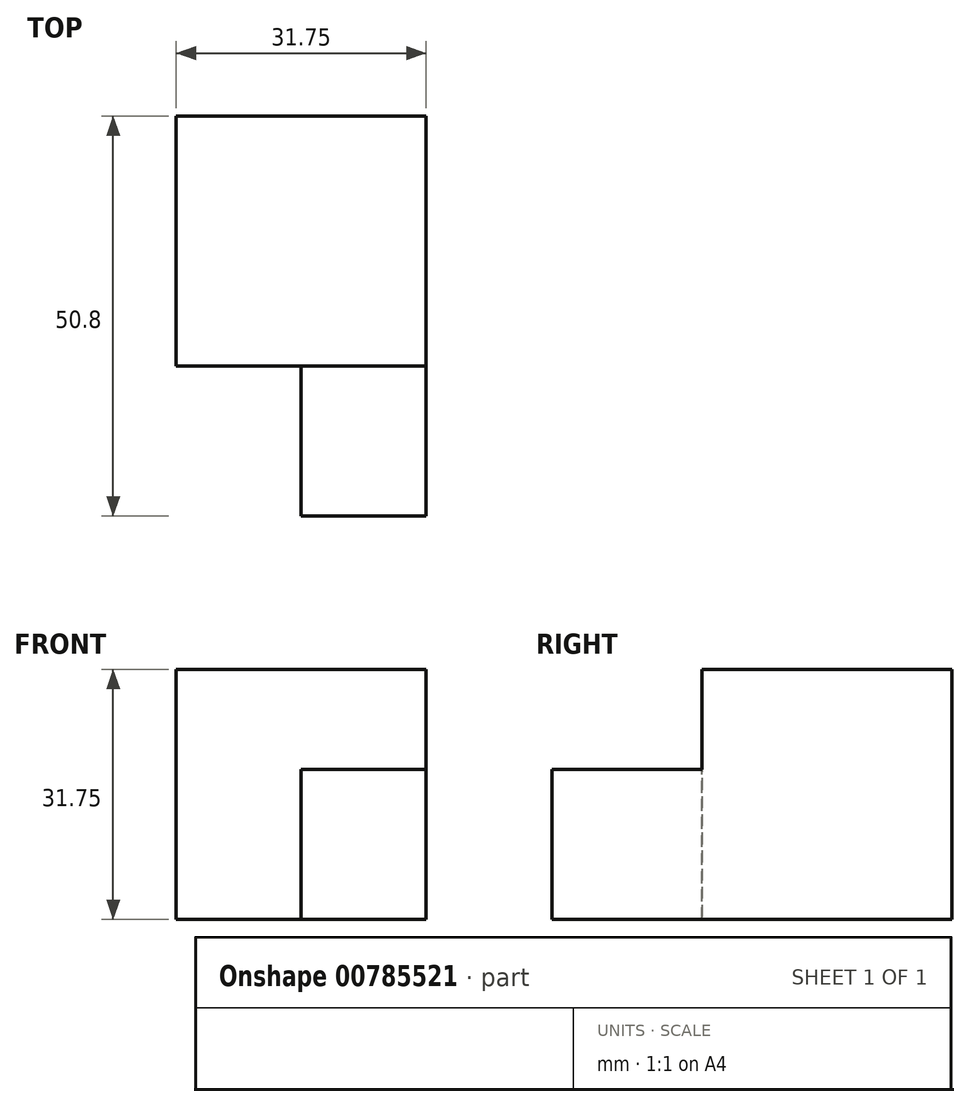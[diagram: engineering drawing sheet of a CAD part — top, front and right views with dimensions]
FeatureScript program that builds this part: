
annotation { "Feature Type Name" : "Feature", "Feature Type Description" : "" }
export const myFeature = defineFeature(function(context is Context, id is Id, definition is map)
    precondition{}
    {
        {
            var Q0;
            Q0=qCreatedBy(makeId("Front.planeOp"),FACE);
            var sketch = newSketch(context, id + "F0", { "sketchPlane" : qUnion([Q0])});
            skLineSegment(sketch, "E0", {"start": v(0, 0) * mm, "end": v(31.75, 0) * mm});
            skLineSegment(sketch, "E1", {"start": v(31.75, 0) * mm, "end": v(31.75, 31.75) * mm});
            skLineSegment(sketch, "E2", {"start": v(31.75, 31.75) * mm, "end": v(0, 31.75) * mm});
            skLineSegment(sketch, "E3", {"start": v(0, 31.75) * mm, "end": v(0, 0) * mm});
            skSolve(sketch);
        }
        {
            var Q0;
            Q0=makeQuery(id+"F0.imprint","IMPRINT",FACE,{"disambiguationData":[TD([[makeQuery(id+"F0.imprint","IMPRINT",EDGE,{"derivedFrom":sQuery(id+"F0.wireOp",EDGE,"E0")}),1.0]])]});
            extrude(context, id + "F1", {"entities" : qUnion([Q0]), "depth" : 50.8 * mm, "offsetDistance" : 25.4 * mm});
        }
        {
            var Q0;
            Q0=makeQuery(id+"F1.opExtrude","CAP_FACE",FACE,{"disambiguationData":[OSD([sQuery(id+"F0.wireOp",EDGE,"E0"),sQuery(id+"F0.wireOp",EDGE,"E1"),sQuery(id+"F0.wireOp",EDGE,"E2"),sQuery(id+"F0.wireOp",EDGE,"E3")])],"isStart":false});
            var sketch = newSketch(context, id + "F2", { "sketchPlane" : qUnion([Q0])});
            skLineSegment(sketch, "E4", {"start": v(31.75, 0) * mm, "end": v(31.75, 19.05) * mm});
            skLineSegment(sketch, "E5", {"start": v(31.75, 19.05) * mm, "end": v(0, 19.05) * mm});
            skSolve(sketch);
        }
        {
            var Q0;
            {var subQ0=sQuery(id+"F2.wireOp",EDGE,"E5");Q0=makeQuery(id+"F2.imprint","IMPRINT",FACE,{"disambiguationData":[TD([[makeQuery(id+"F2.imprint","IMPRINT",EDGE,{"derivedFrom":subQ0}),-1.0]])]});}
            extrude(context, id + "F3", {"entities" : qUnion([Q0]), "operationType" : NewBodyOperationType.REMOVE, "oppositeDirection" : true, "depth" : 19.05 * mm, "offsetDistance" : 25.4 * mm});
        }
        {
            var Q0;
            Q0=makeQuery(id+"F1.opExtrude","CAP_FACE",FACE,{"disambiguationData":[OSD([sQuery(id+"F0.wireOp",EDGE,"E0"),sQuery(id+"F0.wireOp",EDGE,"E1"),sQuery(id+"F0.wireOp",EDGE,"E2"),sQuery(id+"F0.wireOp",EDGE,"E3")])],"isStart":false});
            var sketch = newSketch(context, id + "F4", { "sketchPlane" : qUnion([Q0])});
            skLineSegment(sketch, "E6", {"start": v(31.75, 0) * mm, "end": v(15.88, 0) * mm});
            skLineSegment(sketch, "E7", {"start": v(15.88, 0) * mm, "end": v(15.88, 19.05) * mm});
            skSolve(sketch);
        }
        {
            var Q0;
            {var subQ0=sQuery(id+"F4.wireOp",EDGE,"E7");Q0=makeQuery(id+"F4.imprint","IMPRINT",FACE,{"disambiguationData":[TD([[makeQuery(id+"F4.imprint","IMPRINT",EDGE,{"derivedFrom":subQ0}),1.0]])]});}
            extrude(context, id + "F5", {"entities" : qUnion([Q0]), "operationType" : NewBodyOperationType.REMOVE, "oppositeDirection" : true, "depth" : 19.05 * mm, "offsetDistance" : 25.4 * mm});
        }
    });
